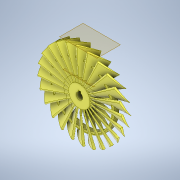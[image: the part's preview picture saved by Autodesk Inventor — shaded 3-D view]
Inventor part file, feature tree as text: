
AUTODESK INVENTOR PART (.ipt)
format: ipt  version: 2021.2 (Build 252289000, 289)  size: 3,321,856 bytes
history: native  units: in
note: dims shown in document units (in); Inventor stores cm internally (conversion verified against a paired STEP export)
features: sketch x6, extrude x4, plane x2, loft x1, pattern_circular x1, revolve x1, other x1
ambient origin geometry x8: Origin, YZ Plane, XZ Plane, XY Plane, X Axis, Y Axis, Z Axis, Center Point
bodies: Solid1 (feature_tree)
feature tree (16):
  extrude  "Extrusion1"  Depth=1.0in
  plane  "Work Plane1"
  plane  "Work Plane2"
  extrude  "Extrusion4"  Depth=2.0in
  loft  "Loft2"
  pattern_circular  "Circular Pattern5"  Count=24 Angle=360.0deg
  extrude  "Extrusion5"  Depth=0.125in
  revolve  "Revolution3"  [1 undecoded]
  extrude  "Extrusion6"  TaperAngle=0.0deg  [1 undecoded]
  sketch  "Sketch1"  dims[d0=1.0in d1=1.0in d2=0.0777in]
  sketch  "Sketch5"  dims[d4=0.75in d15=2.0in]
  sketch  "Sketch6"  dims[d28=0.0312in d29=0.5in d30=0.0in]
  other  "Edges2"
  sketch  "Sketch8"  dims[d31=0.0in d32=90.0deg]
  sketch  "Sketch11"  dims[d33=0.0in d34=90.0deg d35=9.4488in d36=360.0deg]
  sketch  "Sketch12"  dims[d39=0.315in d40=0.125in d41=0.125in d42=0.0in d43=0.0in d54=0.125in d55=0.3in d56=0.05in d57=0.05in d58=0.05in d59=0.05in d60=0.5in d61=0.6in d62=90.0deg d63=3.9375in d64=0.0in d65=0.0in]
note: 2 required parameter values undecoded (feature->parameter linkage not recoverable at this tier; creation-order binding heuristic only, values carry confidence <= 0.55)